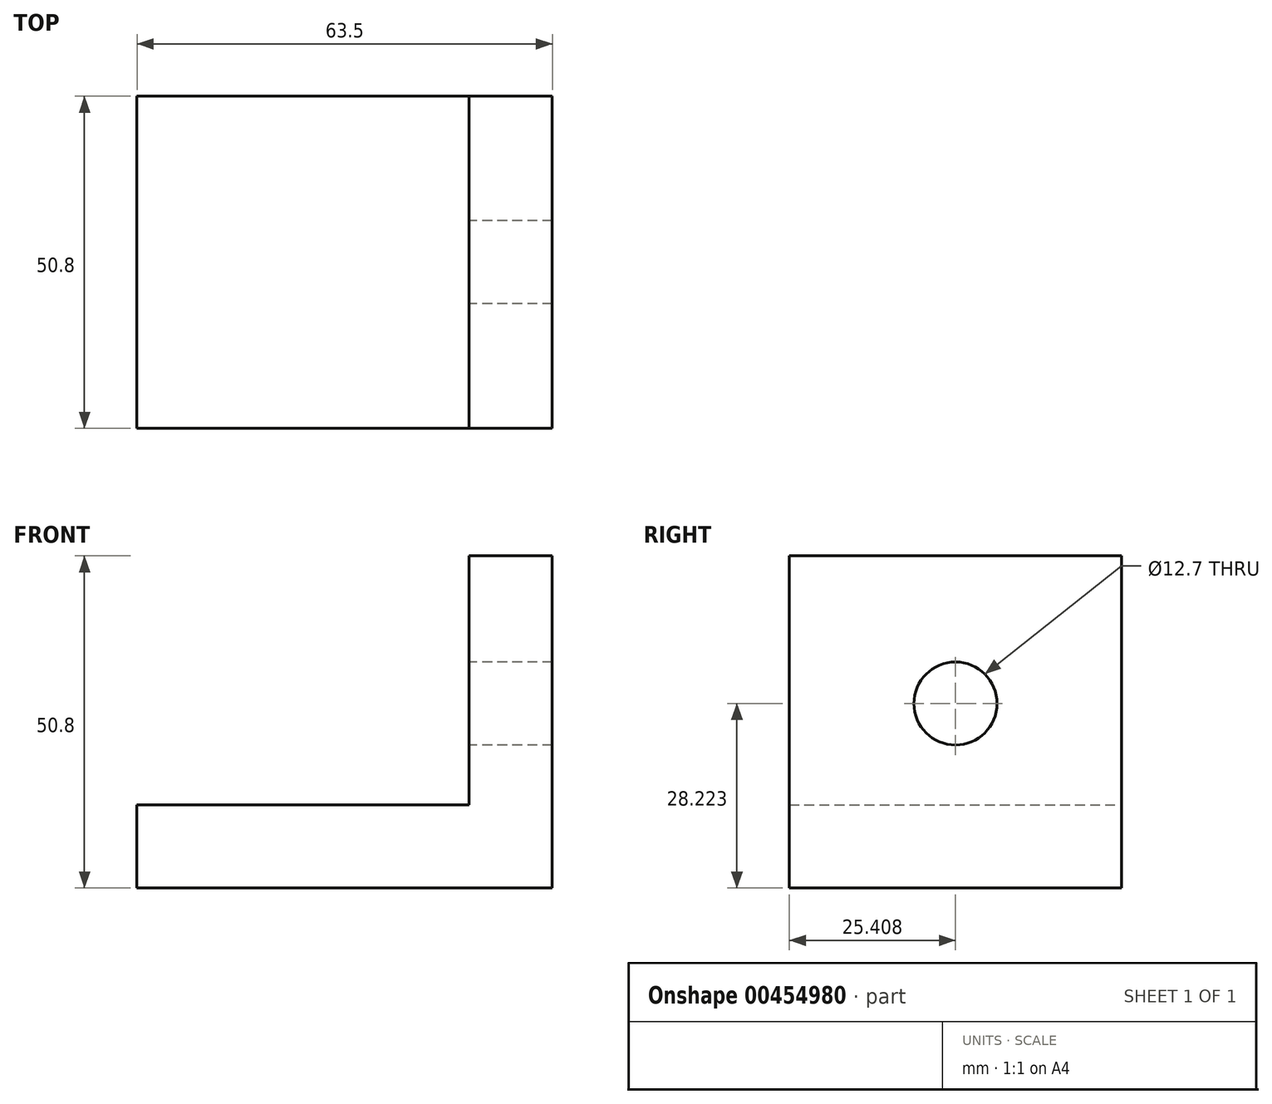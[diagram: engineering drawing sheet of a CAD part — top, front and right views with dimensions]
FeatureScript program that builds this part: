
annotation { "Feature Type Name" : "Feature", "Feature Type Description" : "" }
export const myFeature = defineFeature(function(context is Context, id is Id, definition is map)
    precondition{}
    {
        {
            var Q0;
            Q0=qCreatedBy(makeId("Front.planeOp"),FACE);
            var sketch = newSketch(context, id + "F0", { "sketchPlane" : qUnion([Q0])});
            skLineSegment(sketch, "E0.bottom", {"start": v(-6.68, 50.8) * mm, "end": v(6.02, 50.8) * mm});
            skLineSegment(sketch, "E0.top", {"start": v(-6.68, 0) * mm, "end": v(6.02, 0) * mm});
            skLineSegment(sketch, "E0.left", {"start": v(-6.68, 50.8) * mm, "end": v(-6.68, 0) * mm});
            skLineSegment(sketch, "E0.right", {"start": v(6.02, 50.8) * mm, "end": v(6.02, 0) * mm});
            skSolve(sketch);
        }
        {
            var Q0;
            Q0=makeQuery(id+"F0.imprint","IMPRINT",FACE,{"disambiguationData":[TD([[makeQuery(id+"F0.imprint","IMPRINT",EDGE,{"derivedFrom":sQuery(id+"F0.wireOp",EDGE,"E0.bottom")}),-1.0]])]});
            extrude(context, id + "F1", {"entities" : qUnion([Q0]), "oppositeDirection" : true, "depth" : 50.8 * mm});
        }
        {
            var Q0;
            Q0=makeQuery(id+"F1.opExtrude","SWEPT_FACE",FACE,{"disambiguationData":[OSD([sQuery(id+"F0.wireOp",EDGE,"E0.left")])]});
            var sketch = newSketch(context, id + "F2", { "sketchPlane" : qUnion([Q0])});
            skLineSegment(sketch, "E1", {"start": v(-50.8, 0) * mm, "end": v(-50.8, 12.7) * mm});
            skLineSegment(sketch, "E2", {"start": v(-50.8, 12.7) * mm, "end": v(0, 12.7) * mm});
            skLineSegment(sketch, "E3.bottom", {"start": v(0, 0) * mm, "end": v(-50.8, 0) * mm});
            skLineSegment(sketch, "E3.top", {"start": v(0, 12.7) * mm, "end": v(-50.8, 12.7) * mm});
            skLineSegment(sketch, "E3.left", {"start": v(0, 0) * mm, "end": v(0, 12.7) * mm});
            skSolve(sketch);
        }
        {
            var Q0;
            Q0 = qSketchRegion(id + "F2", true);
            var Q1;
            Q1=makeQuery(id+"F1.opExtrude","SWEPT_FACE",FACE,{"disambiguationData":[OSD([sQuery(id+"F0.wireOp",EDGE,"E0.right")])]});
            extrude(context, id + "F3", {"entities" : qUnion([Q0, Q1]), "operationType" : NewBodyOperationType.ADD, "depth" : 50.8 * mm});
        }
        {
            var Q0;
            Q0=makeQuery(id+"F3.opExtrude","CAP_FACE",FACE,{"disambiguationData":[OSD([sQuery(id+"F0.wireOp",EDGE,"E0.right")])],"isStart":false});
            extrude(context, id + "F4", {"entities" : qUnion([Q0]), "operationType" : NewBodyOperationType.ADD, "oppositeDirection" : true, "depth" : 38.1 * mm});
        }
        {
            var Q0;
            Q0=makeQuery(id+"F3.opExtrude","CAP_FACE",FACE,{"disambiguationData":[OSD([sQuery(id+"F0.wireOp",EDGE,"E0.right")])],"isStart":false});
            extrude(context, id + "F5", {"entities" : qUnion([Q0]), "operationType" : NewBodyOperationType.REMOVE, "oppositeDirection" : true, "depth" : 38.1 * mm});
        }
        {
            var Q0;
            Q0=makeQuery(id+"F5.boolean.opBoolean","COPY",FACE,{"derivedFrom":makeQuery(id+"F5.opExtrude","CAP_FACE",FACE,{"disambiguationData":[OSD([sQuery(id+"F0.wireOp",EDGE,"E0.right")])],"isStart":false})});
            var sketch = newSketch(context, id + "F6", { "sketchPlane" : qUnion([Q0])});
            skCircle(sketch, "E4", {"center": v(-25.4, 28.22) * mm, "radius": 6.35 * mm});
            skSolve(sketch);
        }
        {
            var Q0;
            Q0 = qSketchRegion(id + "F6", true);
            extrude(context, id + "F7", {"entities" : qUnion([Q0]), "operationType" : NewBodyOperationType.REMOVE, "oppositeDirection" : true, "depth" : 25.4 * mm});
        }
    });
